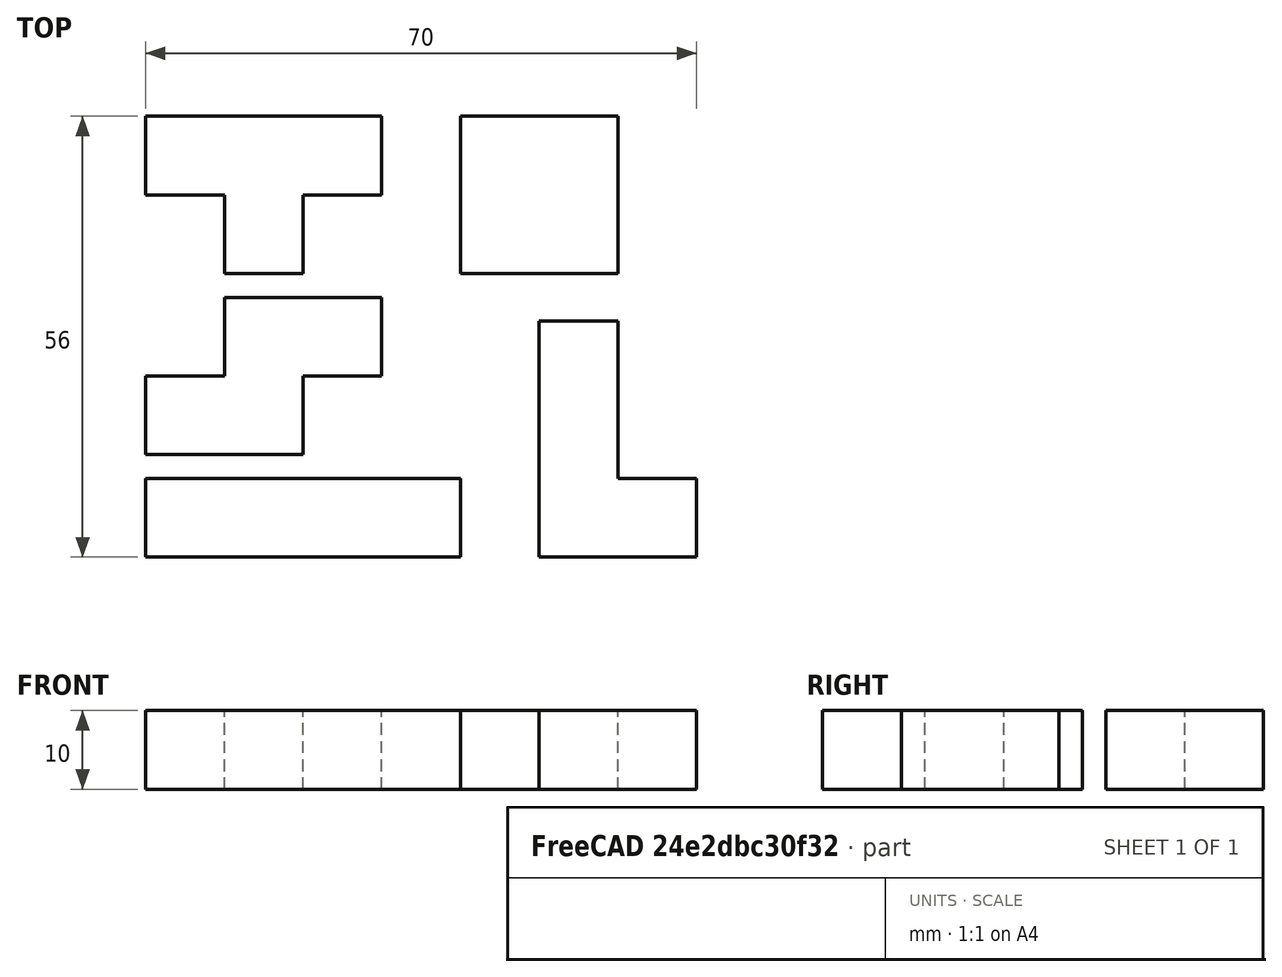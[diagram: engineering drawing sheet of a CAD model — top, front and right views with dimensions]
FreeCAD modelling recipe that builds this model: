
FCSTD DOCUMENT  (FreeCAD 0.21R33694 (Git))
Label: OJT1_T05R03_tetrys
License: All rights reserved
LicenseURL: http://en.wikipedia.org/wiki/All_rights_reserved
objects: Part::Box×13, Part::MultiFuse×4
note: 17 computed .brp shape members not serialized (recipe doc carries the construction recipe); baked Part::Feature solids carry a one-line shape summary decoded from their .brp

FEATURE [Part::Box] Box  label="cubo1"
  AttacherType = Attacher::AttachEngine3D
  Height = 10
  Length = 10
  Width = 10
FEATURE [Part::Box] Box001  label="cubo2"
  AttacherType = Attacher::AttachEngine3D
  Height = 10
  Length = 10
  Placement = pos=(10,0,0) rot=(0,0,1;0rad)
  Width = 10
FEATURE [Part::Box] Box002  label="cubo3"
  AttacherType = Attacher::AttachEngine3D
  Height = 10
  Length = 10
  Placement = pos=(10,10,0) rot=(0,0,1;0rad)
  Width = 10
FEATURE [Part::Box] Box003  label="cubo4"
  AttacherType = Attacher::AttachEngine3D
  Height = 10
  Length = 10
  Placement = pos=(20,10,0) rot=(0,0,1;0rad)
  Width = 10
FEATURE [Part::MultiFuse] Fusion  label="Pieza1"
  Refine = true
  Shapes = -> [Box,Box001,Box002,Box003]
FEATURE [Part::Box] Box004  label="Cube"
  AttacherType = Attacher::AttachEngine3D
  Height = 10
  Length = 10
  Placement = pos=(0,-13,0) rot=(0,0,1;0rad)
  Width = 10
FEATURE [Part::Box] Box005  label="Cube001"
  AttacherType = Attacher::AttachEngine3D
  Height = 10
  Length = 10
  Placement = pos=(10,-13,0) rot=(0,0,1;0rad)
  Width = 10
FEATURE [Part::Box] Box006  label="Cube002"
  AttacherType = Attacher::AttachEngine3D
  Height = 10
  Length = 10
  Placement = pos=(20,-13,0) rot=(0,0,1;0rad)
  Width = 10
FEATURE [Part::Box] Box007  label="Cube003"
  AttacherType = Attacher::AttachEngine3D
  Height = 10
  Length = 10
  Placement = pos=(30,-13,0) rot=(0,0,1;0rad)
  Width = 10
FEATURE [Part::MultiFuse] Fusion001  label="Pieza 2"
  Refine = true
  Shapes = -> [Box007,Box004,Box005,Box006]
FEATURE [Part::Box] Box008  label="Cube004"
  AttacherType = Attacher::AttachEngine3D
  Height = 10
  Length = 20
  Placement = pos=(50,-13,0) rot=(0,0,1;0rad)
  Width = 10
FEATURE [Part::Box] Box009  label="Cube005"
  AttacherType = Attacher::AttachEngine3D
  Height = 10
  Length = 10
  Placement = pos=(50,-3,0) rot=(0,0,1;0rad)
  Width = 20
FEATURE [Part::MultiFuse] Fusion002  label="Pieza3"
  Refine = true
  Shapes = -> [Box009,Box008]
FEATURE [Part::Box] Box010  label="Pieza4"
  AttacherType = Attacher::AttachEngine3D
  Height = 10
  Length = 20
  Placement = pos=(40,23,0) rot=(0,0,1;0rad)
  Width = 20
FEATURE [Part::Box] Box011  label="Cube006"
  AttacherType = Attacher::AttachEngine3D
  Height = 10
  Length = 30
  Placement = pos=(0,33,0) rot=(0,0,1;0rad)
  Width = 10
FEATURE [Part::Box] Box012  label="Cube007"
  AttacherType = Attacher::AttachEngine3D
  Height = 10
  Length = 10
  Placement = pos=(10,23,0) rot=(0,0,1;0rad)
  Width = 10
FEATURE [Part::MultiFuse] Fusion003  label="Pieza5"
  Refine = true
  Shapes = -> [Box012,Box011]
